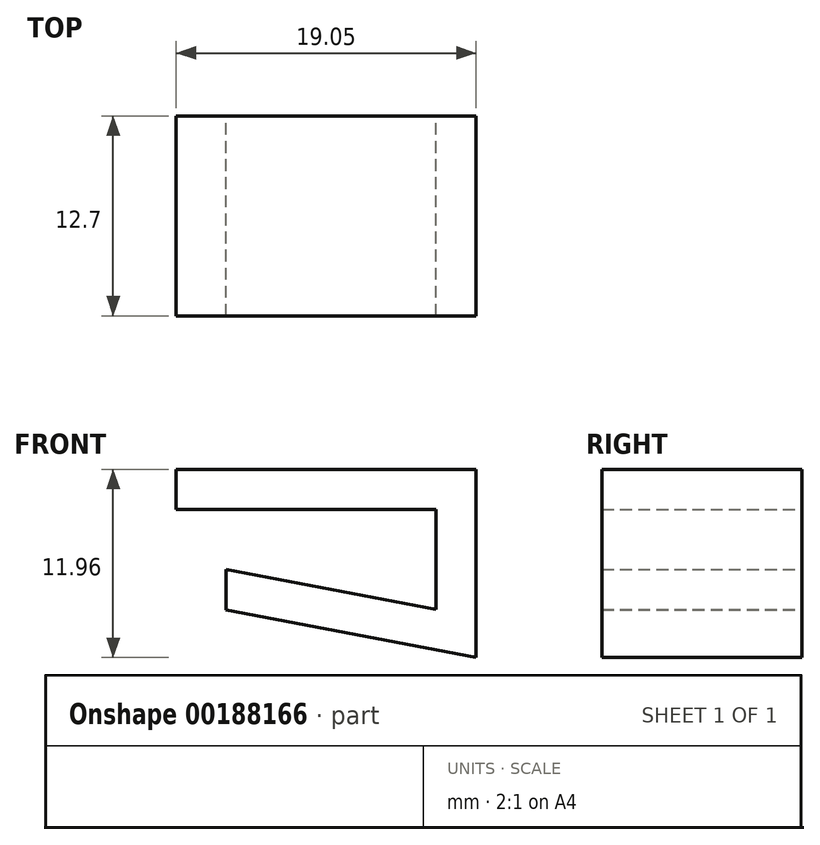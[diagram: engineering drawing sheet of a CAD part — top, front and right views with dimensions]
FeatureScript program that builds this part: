
annotation { "Feature Type Name" : "Feature", "Feature Type Description" : "" }
export const myFeature = defineFeature(function(context is Context, id is Id, definition is map)
    precondition{}
    {
        {
            var Q0;
            Q0=qCreatedBy(makeId("Front.planeOp"),FACE);
            var sketch = newSketch(context, id + "F0", { "sketchPlane" : qUnion([Q0])});
            skLineSegment(sketch, "E0", {"start": v(3.17, -6.35) * mm, "end": v(16.5, -8.89) * mm});
            skLineSegment(sketch, "E1", {"start": v(16.51, -8.89) * mm, "end": v(16.51, -2.54) * mm});
            skLineSegment(sketch, "E2", {"start": v(16.5, -2.54) * mm, "end": v(0, -2.54) * mm});
            skLineSegment(sketch, "E3.1", {"start": v(3.17, -8.94) * mm, "end": v(19.05, -11.96) * mm});
            skLineSegment(sketch, "E3.2", {"start": v(19.05, -11.96) * mm, "end": v(19.05, 0) * mm});
            skLineSegment(sketch, "E3.3", {"start": v(19.05, 0) * mm, "end": v(0, 0) * mm});
            skLineSegment(sketch, "E4", {"start": v(3.18, -6.35) * mm, "end": v(3.18, -8.94) * mm});
            skLineSegment(sketch, "E5", {"start": v(0, 0) * mm, "end": v(0, -2.54) * mm});
            skSolve(sketch);
        }
        {
            var Q0;
            Q0 = qSketchRegion(id + "F0", true);
            extrude(context, id + "F1", {"entities" : qUnion([Q0]), "depth" : 12.7 * mm});
        }
    });
